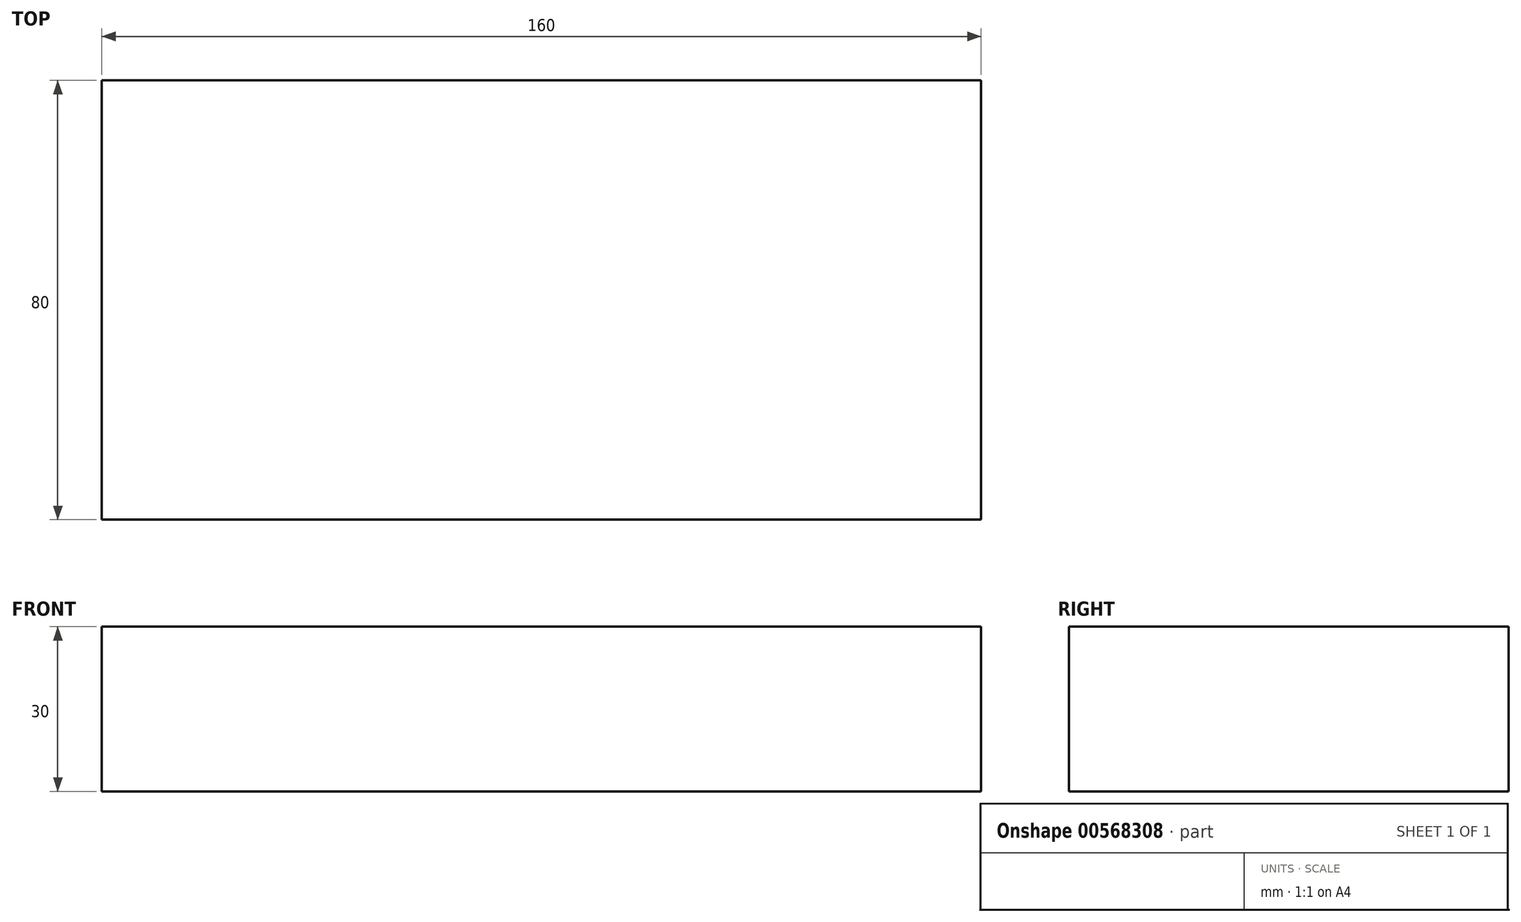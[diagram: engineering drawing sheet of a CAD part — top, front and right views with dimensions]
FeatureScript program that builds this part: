
annotation { "Feature Type Name" : "Feature", "Feature Type Description" : "" }
export const myFeature = defineFeature(function(context is Context, id is Id, definition is map)
    precondition{}
    {
        {
            var Q0;
            Q0=qCreatedBy(makeId("Top.planeOp"),FACE);
            var sketch = newSketch(context, id + "F0", { "sketchPlane" : qUnion([Q0])});
            skLineSegment(sketch, "E0.bottom", {"start": v(-80, 40) * mm, "end": v(80, 40) * mm});
            skLineSegment(sketch, "E0.top", {"start": v(-80, -40) * mm, "end": v(80, -40) * mm});
            skLineSegment(sketch, "E0.left", {"start": v(-80, 40) * mm, "end": v(-80, -40) * mm});
            skLineSegment(sketch, "E0.right", {"start": v(80, 40) * mm, "end": v(80, -40) * mm});
            skPoint(sketch, "E0.middle", {"position": v(0, 0) * mm});
            skSolve(sketch);
        }
        {
            var Q0;
            Q0=makeQuery(id+"F0.imprint","IMPRINT",FACE,{"disambiguationData":[TD([[makeQuery(id+"F0.imprint","IMPRINT",EDGE,{"derivedFrom":sQuery(id+"F0.wireOp",EDGE,"E0.bottom")}),-1.0]])]});
            extrude(context, id + "F1", {"entities" : qUnion([Q0]), "depth" : 30 * mm, "offsetDistance" : 25 * mm});
        }
    });
